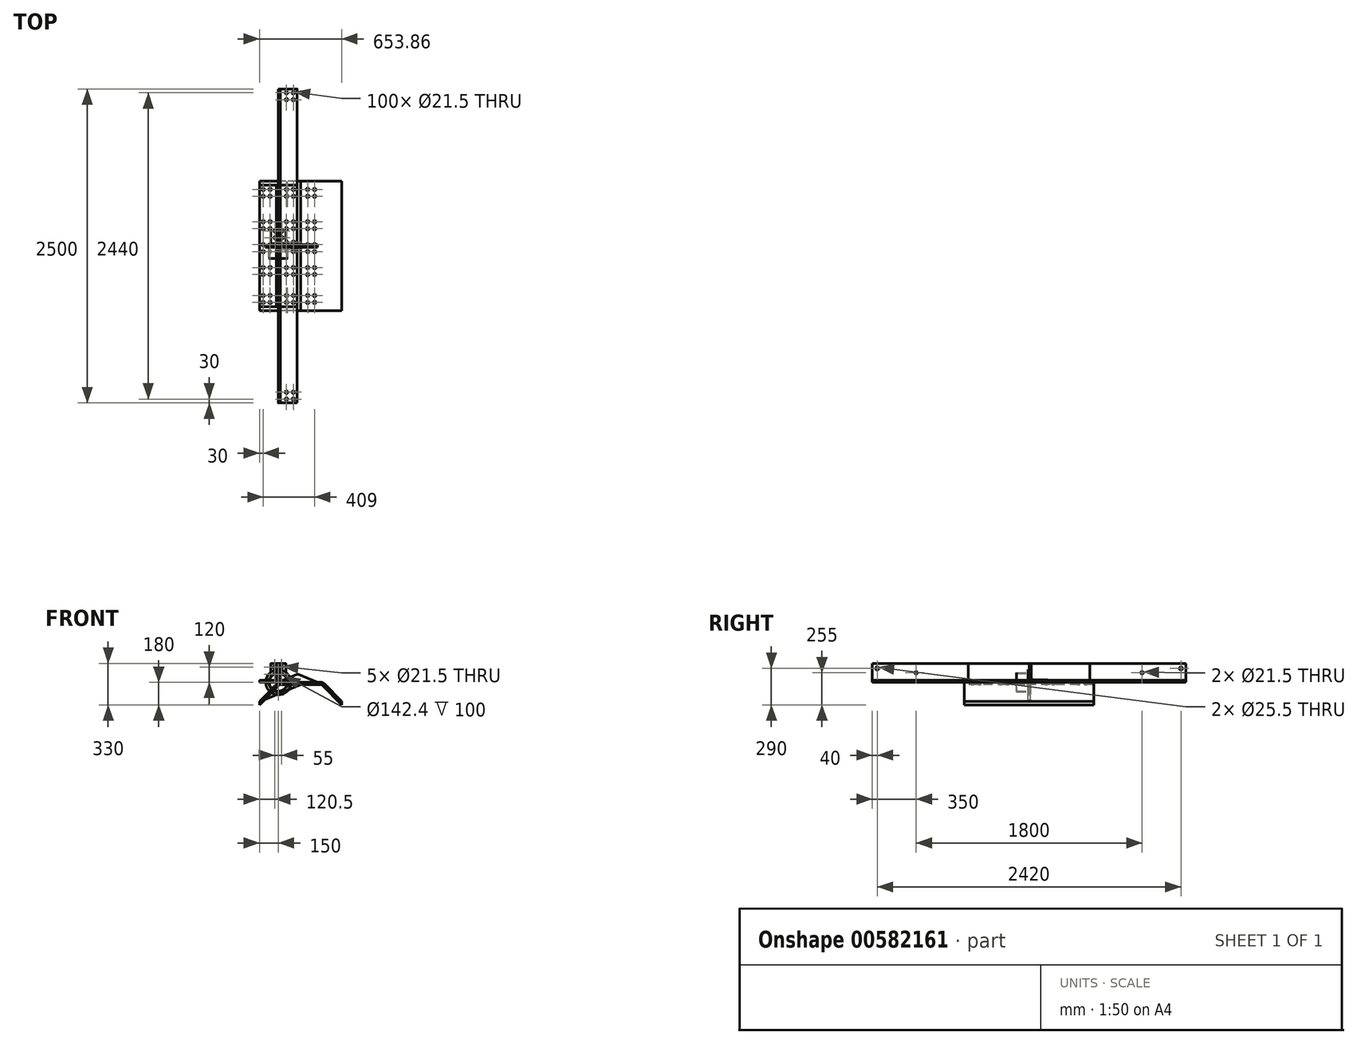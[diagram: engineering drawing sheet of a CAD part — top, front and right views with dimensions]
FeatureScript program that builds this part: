
annotation { "Feature Type Name" : "Feature", "Feature Type Description" : "" }
export const myFeature = defineFeature(function(context is Context, id is Id, definition is map)
    precondition{}
    {
        {
            var Q0;
            Q0=qCreatedBy(makeId("Front.planeOp"),FACE);
            var sketch = newSketch(context, id + "F0", { "sketchPlane" : qUnion([Q0])});
            skLineSegment(sketch, "E0", {"start": v(0, 0) * mm, "end": v(0, 145) * mm});
            skLineSegment(sketch, "E1", {"start": v(0, 0) * mm, "end": v(145, 0) * mm});
            skLineSegment(sketch, "E2", {"start": v(150, 5) * mm, "end": v(150, 10) * mm});
            skLineSegment(sketch, "E3", {"start": v(145, 15) * mm, "end": v(35, 15) * mm});
            skLineSegment(sketch, "E4", {"start": v(15, 35) * mm, "end": v(15, 145) * mm});
            skLineSegment(sketch, "E5", {"start": v(10, 150) * mm, "end": v(5, 150) * mm});
            skPoint(sketch, "E6.visualSharp", {"position": v(15, 15) * mm});
            skArc(sketch, "E6.filletArc", {"start": v(15, 35) * mm, "mid": v(20.86, 20.86) * mm, "end": v(35, 15) * mm});
            skPoint(sketch, "E7.visualSharp", {"position": v(0, 150) * mm});
            skArc(sketch, "E7.filletArc", {"start": v(5, 150) * mm, "mid": v(1.46, 148.54) * mm, "end": v(0, 145) * mm});
            skPoint(sketch, "E8.visualSharp", {"position": v(15, 150) * mm});
            skArc(sketch, "E8.filletArc", {"start": v(15, 145) * mm, "mid": v(13.54, 148.54) * mm, "end": v(10, 150) * mm});
            skPoint(sketch, "E9.visualSharp", {"position": v(150, 15) * mm});
            skArc(sketch, "E9.filletArc", {"start": v(150, 10) * mm, "mid": v(148.54, 13.54) * mm, "end": v(145, 15) * mm});
            skPoint(sketch, "E10.visualSharp", {"position": v(150, 0) * mm});
            skArc(sketch, "E10.filletArc", {"start": v(145, 0) * mm, "mid": v(148.54, 1.46) * mm, "end": v(150, 5) * mm});
            skSolve(sketch);
        }
        {
            var Q0;
            Q0=makeQuery(id+"F0.imprint","IMPRINT",FACE,{"disambiguationData":[TD([[makeQuery(id+"F0.imprint","IMPRINT",EDGE,{"derivedFrom":sQuery(id+"F0.wireOp",EDGE,"E0")}),-1.0]])]});
            extrude(context, id + "F1", {"entities" : qUnion([Q0]), "endBound" : BoundingType.SYMMETRIC, "depth" : 968 * mm, "offsetDistance" : 25 * mm});
        }
        {
            var Q0;
            Q0=qCreatedBy(makeId("Top.planeOp"),FACE);
            var sketch = newSketch(context, id + "F2", { "sketchPlane" : qUnion([Q0])});
            skLineSegment(sketch, "E11", {"start": v(65, -476.9) * mm, "end": v(65, 500.9) * mm});
            skLineSegment(sketch, "E12", {"start": v(120, -552.3) * mm, "end": v(120, 547.64) * mm});
            skLineSegment(sketch, "E13", {"start": v(184.91, -450) * mm, "end": v(-39.38, -450) * mm});
            skLineSegment(sketch, "E14", {"start": v(-37.47, -395) * mm, "end": v(183, -395) * mm});
            skLineSegment(sketch, "E15", {"start": v(183.02, -227.5) * mm, "end": v(-41.27, -227.5) * mm});
            skLineSegment(sketch, "E16", {"start": v(-39.36, -172.5) * mm, "end": v(181.1, -172.5) * mm});
            skLineSegment(sketch, "E17", {"start": v(186.82, 137.5) * mm, "end": v(-37.47, 137.5) * mm});
            skLineSegment(sketch, "E18", {"start": v(-35.56, 192.5) * mm, "end": v(184.91, 192.5) * mm});
            skLineSegment(sketch, "E19", {"start": v(181.72, 395) * mm, "end": v(-42.57, 395) * mm});
            skLineSegment(sketch, "E20", {"start": v(-40.66, 450) * mm, "end": v(179.8, 450) * mm});
            skLineSegment(sketch, "E21", {"start": v(184.27, -45) * mm, "end": v(-40.03, -45) * mm});
            skLineSegment(sketch, "E22", {"start": v(-38.11, 10) * mm, "end": v(182.36, 10) * mm});
            skPoint(sketch, "E23", {"position": v(65, -450) * mm});
            skPoint(sketch, "E24", {"position": v(120, -450) * mm});
            skPoint(sketch, "E25", {"position": v(120, -395) * mm});
            skPoint(sketch, "E26", {"position": v(65, -395) * mm});
            skPoint(sketch, "E27", {"position": v(65, -227.5) * mm});
            skPoint(sketch, "E28", {"position": v(120, -227.5) * mm});
            skPoint(sketch, "E29", {"position": v(120, -172.5) * mm});
            skPoint(sketch, "E30", {"position": v(65, -172.5) * mm});
            skPoint(sketch, "E31", {"position": v(65, -45) * mm});
            skPoint(sketch, "E32", {"position": v(120, -45) * mm});
            skPoint(sketch, "E33", {"position": v(65, 10) * mm});
            skPoint(sketch, "E34", {"position": v(120, 10) * mm});
            skPoint(sketch, "E35", {"position": v(65, 137.5) * mm});
            skPoint(sketch, "E36", {"position": v(65, 192.5) * mm});
            skPoint(sketch, "E37", {"position": v(120, 192.5) * mm});
            skPoint(sketch, "E38", {"position": v(120, 137.5) * mm});
            skPoint(sketch, "E39", {"position": v(65, 395) * mm});
            skPoint(sketch, "E40", {"position": v(120, 395) * mm});
            skPoint(sketch, "E41", {"position": v(120, 450) * mm});
            skPoint(sketch, "E42", {"position": v(65, 450) * mm});
            skSolve(sketch);
        }
        {
            var Q0;
            Q0=sQuery(id+"F2.wireOp",VERTEX,"E23");
            var Q1;
            Q1=sQuery(id+"F2.wireOp",VERTEX,"E26");
            var Q2;
            Q2=sQuery(id+"F2.wireOp",VERTEX,"E25");
            var Q3;
            Q3=sQuery(id+"F2.wireOp",VERTEX,"E24");
            var Q4;
            Q4=sQuery(id+"F2.wireOp",VERTEX,"E27");
            var Q5;
            Q5=sQuery(id+"F2.wireOp",VERTEX,"E28");
            var Q6;
            Q6=sQuery(id+"F2.wireOp",VERTEX,"E29");
            var Q7;
            Q7=sQuery(id+"F2.wireOp",VERTEX,"E30");
            var Q8;
            Q8=sQuery(id+"F2.wireOp",VERTEX,"E31");
            var Q9;
            Q9=sQuery(id+"F2.wireOp",VERTEX,"E33");
            var Q10;
            Q10=sQuery(id+"F2.wireOp",VERTEX,"E34");
            var Q11;
            Q11=sQuery(id+"F2.wireOp",VERTEX,"E32");
            var Q12;
            Q12=sQuery(id+"F2.wireOp",VERTEX,"E35");
            var Q13;
            Q13=sQuery(id+"F2.wireOp",VERTEX,"E38");
            var Q14;
            Q14=sQuery(id+"F2.wireOp",VERTEX,"E37");
            var Q15;
            Q15=sQuery(id+"F2.wireOp",VERTEX,"E36");
            var Q16;
            Q16=sQuery(id+"F2.wireOp",VERTEX,"E39");
            var Q17;
            Q17=sQuery(id+"F2.wireOp",VERTEX,"E40");
            var Q18;
            Q18=sQuery(id+"F2.wireOp",VERTEX,"E42");
            var Q19;
            Q19=sQuery(id+"F2.wireOp",VERTEX,"E41");
            var Q20;
            Q20=makeQuery(id+"F1.opExtrude","SWEPT_BODY",BODY,{"disambiguationData":[OSD([sQuery(id+"F0.wireOp",EDGE,"E0"),sQuery(id+"F0.wireOp",EDGE,"E1"),sQuery(id+"F0.wireOp",EDGE,"E2"),sQuery(id+"F0.wireOp",EDGE,"E3"),sQuery(id+"F0.wireOp",EDGE,"E4"),sQuery(id+"F0.wireOp",EDGE,"E5"),sQuery(id+"F0.wireOp",EDGE,"E6.filletArc"),sQuery(id+"F0.wireOp",EDGE,"E7.filletArc"),sQuery(id+"F0.wireOp",EDGE,"E8.filletArc"),sQuery(id+"F0.wireOp",EDGE,"E9.filletArc"),sQuery(id+"F0.wireOp",EDGE,"E10.filletArc")])]});
            hole(context, id + "F3", {"style" : HoleStyle.SIMPLE, "endStyle" : HoleEndStyle.THROUGH, "oppositeDirection" : true, "holeDiameter" : 21.5 * mm, "majorDiameter" : 5 * mm, "isTappedThrough" : true, "tappedDepth" : 12 * mm, "tapClearance" : 3, "startFromSketch" : true, "locations" : qUnion([Q0, Q1, Q2, Q3, Q4, Q5, Q6, Q7, Q8, Q9, Q10, Q11, Q12, Q13, Q14, Q15, Q16, Q17, Q18, Q19]), "scope" : qUnion([Q20])});
        }
        {
            var Q0;
            Q0=makeQuery(id+"F1.opExtrude","SWEPT_BODY",BODY,{"disambiguationData":[OSD([sQuery(id+"F0.wireOp",EDGE,"E0"),sQuery(id+"F0.wireOp",EDGE,"E1"),sQuery(id+"F0.wireOp",EDGE,"E2"),sQuery(id+"F0.wireOp",EDGE,"E3"),sQuery(id+"F0.wireOp",EDGE,"E4"),sQuery(id+"F0.wireOp",EDGE,"E5"),sQuery(id+"F0.wireOp",EDGE,"E6.filletArc"),sQuery(id+"F0.wireOp",EDGE,"E7.filletArc"),sQuery(id+"F0.wireOp",EDGE,"E8.filletArc"),sQuery(id+"F0.wireOp",EDGE,"E9.filletArc"),sQuery(id+"F0.wireOp",EDGE,"E10.filletArc")])]});
            var Q1;
            Q1=qCreatedBy(makeId("Right.planeOp"),FACE);
            mirror(context, id + "F4", {"entities" : qUnion([Q0]), "mirrorPlane" : qUnion([Q1])});
        }
        {
            var Q0;
            Q0=makeQuery(id+"F1.opExtrude","SWEPT_BODY",BODY,{"disambiguationData":[OSD([sQuery(id+"F0.wireOp",EDGE,"E0"),sQuery(id+"F0.wireOp",EDGE,"E1"),sQuery(id+"F0.wireOp",EDGE,"E2"),sQuery(id+"F0.wireOp",EDGE,"E3"),sQuery(id+"F0.wireOp",EDGE,"E4"),sQuery(id+"F0.wireOp",EDGE,"E5"),sQuery(id+"F0.wireOp",EDGE,"E6.filletArc"),sQuery(id+"F0.wireOp",EDGE,"E7.filletArc"),sQuery(id+"F0.wireOp",EDGE,"E8.filletArc"),sQuery(id+"F0.wireOp",EDGE,"E9.filletArc"),sQuery(id+"F0.wireOp",EDGE,"E10.filletArc")])]});
            transform(context, id + "F5", {"entities" : qUnion([Q0]), "transformType" : TransformType.TRANSLATION_3D, "dx" : 500 * mm, "dy" : 0 * mm, "dz" : 0 * mm, "makeCopy" : true});
        }
        {
            var Q0;
            Q0=makeQuery(id+"F5.opPattern","COPY",BODY,{"derivedFrom":makeQuery(id+"F1.opExtrude","SWEPT_BODY",BODY,{"disambiguationData":[OSD([sQuery(id+"F0.wireOp",EDGE,"E0"),sQuery(id+"F0.wireOp",EDGE,"E1"),sQuery(id+"F0.wireOp",EDGE,"E2"),sQuery(id+"F0.wireOp",EDGE,"E3"),sQuery(id+"F0.wireOp",EDGE,"E4"),sQuery(id+"F0.wireOp",EDGE,"E5"),sQuery(id+"F0.wireOp",EDGE,"E6.filletArc"),sQuery(id+"F0.wireOp",EDGE,"E7.filletArc"),sQuery(id+"F0.wireOp",EDGE,"E8.filletArc"),sQuery(id+"F0.wireOp",EDGE,"E9.filletArc"),sQuery(id+"F0.wireOp",EDGE,"E10.filletArc")])]}),"instanceName":"1"});
            deleteBodies(context, id + "F6", {"entities" : qUnion([Q0])});
        }
        {
            var Q0;
            Q0=makeQuery(id+"F0.imprint","IMPRINT",FACE,{"disambiguationData":[TD([[makeQuery(id+"F0.imprint","IMPRINT",EDGE,{"derivedFrom":sQuery(id+"F0.wireOp",EDGE,"E0")}),-1.0]])]});
            extrude(context, id + "F7", {"entities" : qUnion([Q0]), "endBound" : BoundingType.SYMMETRIC, "depth" : 2500 * mm, "offsetDistance" : 25 * mm});
        }
        {
            var Q0;
            Q0=qCreatedBy(makeId("Top.planeOp"),FACE);
            var sketch = newSketch(context, id + "F8", { "sketchPlane" : qUnion([Q0])});
            skLineSegment(sketch, "E43", {"start": v(65, -1246.9) * mm, "end": v(65, 1291.05) * mm});
            skLineSegment(sketch, "E44", {"start": v(120, -1322.3) * mm, "end": v(120, 1283.3) * mm});
            skLineSegment(sketch, "E45", {"start": v(195.65, -1220) * mm, "end": v(-28.65, -1220) * mm});
            skLineSegment(sketch, "E46", {"start": v(-26.74, -1165) * mm, "end": v(193.74, -1165) * mm});
            skPoint(sketch, "E47", {"position": v(65, -1220) * mm});
            skPoint(sketch, "E48", {"position": v(120, -1220) * mm});
            skPoint(sketch, "E49", {"position": v(120, -1165) * mm});
            skPoint(sketch, "E50", {"position": v(65, -1165) * mm});
            skLineSegment(sketch, "E51", {"start": v(195.65, -30) * mm, "end": v(-28.65, -30) * mm});
            skLineSegment(sketch, "E52", {"start": v(-26.74, 30) * mm, "end": v(193.74, 30) * mm});
            skPoint(sketch, "E53", {"position": v(65, -30) * mm});
            skPoint(sketch, "E54", {"position": v(120, -30) * mm});
            skPoint(sketch, "E55", {"position": v(120, 30) * mm});
            skPoint(sketch, "E56", {"position": v(65, 30) * mm});
            skLineSegment(sketch, "E57", {"start": v(195.65, 1165) * mm, "end": v(-28.65, 1165) * mm});
            skLineSegment(sketch, "E58", {"start": v(-26.74, 1220) * mm, "end": v(193.74, 1220) * mm});
            skPoint(sketch, "E59", {"position": v(65, 1165) * mm});
            skPoint(sketch, "E60", {"position": v(120, 1165) * mm});
            skPoint(sketch, "E61", {"position": v(120, 1220) * mm});
            skPoint(sketch, "E62", {"position": v(65, 1220) * mm});
            skSolve(sketch);
        }
        {
            var Q0;
            Q0=sQuery(id+"F8.wireOp",VERTEX,"E48");
            var Q1;
            Q1=sQuery(id+"F8.wireOp",VERTEX,"E47");
            var Q2;
            Q2=sQuery(id+"F8.wireOp",VERTEX,"E50");
            var Q3;
            Q3=sQuery(id+"F8.wireOp",VERTEX,"E49");
            var Q4;
            Q4=sQuery(id+"F8.wireOp",VERTEX,"E53");
            var Q5;
            Q5=sQuery(id+"F8.wireOp",VERTEX,"E56");
            var Q6;
            Q6=sQuery(id+"F8.wireOp",VERTEX,"E55");
            var Q7;
            Q7=sQuery(id+"F8.wireOp",VERTEX,"E54");
            var Q8;
            Q8=sQuery(id+"F8.wireOp",VERTEX,"E62");
            var Q9;
            Q9=sQuery(id+"F8.wireOp",VERTEX,"E61");
            var Q10;
            Q10=sQuery(id+"F8.wireOp",VERTEX,"E60");
            var Q11;
            Q11=sQuery(id+"F8.wireOp",VERTEX,"E59");
            var Q12;
            Q12=makeQuery(id+"F7.opExtrude","SWEPT_BODY",BODY,{"disambiguationData":[OSD([sQuery(id+"F0.wireOp",EDGE,"E0"),sQuery(id+"F0.wireOp",EDGE,"E1"),sQuery(id+"F0.wireOp",EDGE,"E2"),sQuery(id+"F0.wireOp",EDGE,"E3"),sQuery(id+"F0.wireOp",EDGE,"E4"),sQuery(id+"F0.wireOp",EDGE,"E5"),sQuery(id+"F0.wireOp",EDGE,"E6.filletArc"),sQuery(id+"F0.wireOp",EDGE,"E7.filletArc"),sQuery(id+"F0.wireOp",EDGE,"E8.filletArc"),sQuery(id+"F0.wireOp",EDGE,"E9.filletArc"),sQuery(id+"F0.wireOp",EDGE,"E10.filletArc")])]});
            hole(context, id + "F9", {"style" : HoleStyle.SIMPLE, "endStyle" : HoleEndStyle.THROUGH, "oppositeDirection" : true, "holeDiameter" : 21.5 * mm, "majorDiameter" : 5 * mm, "isTappedThrough" : true, "tappedDepth" : 12 * mm, "tapClearance" : 3, "startFromSketch" : true, "locations" : qUnion([Q0, Q1, Q2, Q3, Q4, Q5, Q6, Q7, Q8, Q9, Q10, Q11]), "scope" : qUnion([Q12])});
        }
        {
            var Q0;
            Q0=qCreatedBy(makeId("Right.planeOp"),FACE);
            var sketch = newSketch(context, id + "F10", { "sketchPlane" : qUnion([Q0])});
            skLineSegment(sketch, "E63", {"start": v(-1210, 110) * mm, "end": v(-1210, 75) * mm});
            skLineSegment(sketch, "E64", {"start": v(-1210, 75) * mm, "end": v(-900, 75) * mm});
            skLineSegment(sketch, "E65", {"start": v(-900, 75) * mm, "end": v(-900, 110) * mm});
            skLineSegment(sketch, "E66", {"start": v(-900, 110) * mm, "end": v(900, 110) * mm});
            skLineSegment(sketch, "E67", {"start": v(900, 110) * mm, "end": v(900, 75) * mm});
            skLineSegment(sketch, "E68", {"start": v(900, 75) * mm, "end": v(1210, 75) * mm});
            skLineSegment(sketch, "E69", {"start": v(1210, 75) * mm, "end": v(1210, 110) * mm});
            skPoint(sketch, "E70", {"position": v(-1210, 110) * mm});
            skPoint(sketch, "E71", {"position": v(-900, 75) * mm});
            skPoint(sketch, "E72", {"position": v(900, 75) * mm});
            skPoint(sketch, "E73", {"position": v(1210, 110) * mm});
            skSolve(sketch);
        }
        {
            var Q0;
            Q0=sQuery(id+"F10.wireOp",VERTEX,"E68.start");
            var Q1;
            Q1=sQuery(id+"F10.wireOp",VERTEX,"E71");
            var Q2;
            Q2=makeQuery(id+"F7.opExtrude","SWEPT_BODY",BODY,{"disambiguationData":[OSD([sQuery(id+"F0.wireOp",EDGE,"E0"),sQuery(id+"F0.wireOp",EDGE,"E1"),sQuery(id+"F0.wireOp",EDGE,"E2"),sQuery(id+"F0.wireOp",EDGE,"E3"),sQuery(id+"F0.wireOp",EDGE,"E4"),sQuery(id+"F0.wireOp",EDGE,"E5"),sQuery(id+"F0.wireOp",EDGE,"E6.filletArc"),sQuery(id+"F0.wireOp",EDGE,"E7.filletArc"),sQuery(id+"F0.wireOp",EDGE,"E8.filletArc"),sQuery(id+"F0.wireOp",EDGE,"E9.filletArc"),sQuery(id+"F0.wireOp",EDGE,"E10.filletArc")])]});
            hole(context, id + "F11", {"style" : HoleStyle.SIMPLE, "endStyle" : HoleEndStyle.THROUGH, "oppositeDirection" : true, "holeDiameter" : 21.5 * mm, "majorDiameter" : 5 * mm, "isTappedThrough" : true, "tappedDepth" : 12 * mm, "tapClearance" : 3, "startFromSketch" : true, "locations" : qUnion([Q0, Q1]), "scope" : qUnion([Q2])});
        }
        {
            var Q0;
            Q0=sQuery(id+"F10.wireOp",VERTEX,"E63.start");
            var Q1;
            Q1=sQuery(id+"F10.wireOp",VERTEX,"E73");
            var Q2;
            Q2=makeQuery(id+"F7.opExtrude","SWEPT_BODY",BODY,{"disambiguationData":[OSD([sQuery(id+"F0.wireOp",EDGE,"E0"),sQuery(id+"F0.wireOp",EDGE,"E1"),sQuery(id+"F0.wireOp",EDGE,"E2"),sQuery(id+"F0.wireOp",EDGE,"E3"),sQuery(id+"F0.wireOp",EDGE,"E4"),sQuery(id+"F0.wireOp",EDGE,"E5"),sQuery(id+"F0.wireOp",EDGE,"E6.filletArc"),sQuery(id+"F0.wireOp",EDGE,"E7.filletArc"),sQuery(id+"F0.wireOp",EDGE,"E8.filletArc"),sQuery(id+"F0.wireOp",EDGE,"E9.filletArc"),sQuery(id+"F0.wireOp",EDGE,"E10.filletArc")])]});
            hole(context, id + "F12", {"style" : HoleStyle.SIMPLE, "endStyle" : HoleEndStyle.THROUGH, "oppositeDirection" : true, "holeDiameter" : 25.5 * mm, "majorDiameter" : 5 * mm, "isTappedThrough" : true, "tappedDepth" : 12 * mm, "tapClearance" : 3, "startFromSketch" : true, "locations" : qUnion([Q0, Q1]), "scope" : qUnion([Q2])});
        }
        {
            var Q0;
            Q0=qCreatedBy(makeId("Front.planeOp"),FACE);
            var sketch = newSketch(context, id + "F13", { "sketchPlane" : qUnion([Q0])});
            skLineSegment(sketch, "E74", {"start": v(0, 97) * mm, "end": v(0, 0) * mm});
            skLineSegment(sketch, "E75", {"start": v(0, 0) * mm, "end": v(97, 0) * mm});
            skLineSegment(sketch, "E76", {"start": v(100, 3) * mm, "end": v(100, 7) * mm});
            skLineSegment(sketch, "E77", {"start": v(97, 10) * mm, "end": v(22, 10) * mm});
            skLineSegment(sketch, "E78", {"start": v(10, 22) * mm, "end": v(10, 97) * mm});
            skLineSegment(sketch, "E79", {"start": v(7, 100) * mm, "end": v(3, 100) * mm});
            skPoint(sketch, "E80.visualSharp", {"position": v(0, 100) * mm});
            skArc(sketch, "E80.filletArc", {"start": v(3, 100) * mm, "mid": v(0.88, 99.12) * mm, "end": v(0, 97) * mm});
            skPoint(sketch, "E81.visualSharp", {"position": v(10, 100) * mm});
            skArc(sketch, "E81.filletArc", {"start": v(10, 97) * mm, "mid": v(9.12, 99.12) * mm, "end": v(7, 100) * mm});
            skPoint(sketch, "E82.visualSharp", {"position": v(100, 10) * mm});
            skArc(sketch, "E82.filletArc", {"start": v(100, 7) * mm, "mid": v(99.12, 9.12) * mm, "end": v(97, 10) * mm});
            skPoint(sketch, "E83.visualSharp", {"position": v(100, 0) * mm});
            skArc(sketch, "E83.filletArc", {"start": v(97, 0) * mm, "mid": v(99.12, 0.88) * mm, "end": v(100, 3) * mm});
            skPoint(sketch, "E84.visualSharp", {"position": v(10, 10) * mm});
            skArc(sketch, "E84.filletArc", {"start": v(10, 22) * mm, "mid": v(13.51, 13.51) * mm, "end": v(22, 10) * mm});
            skSolve(sketch);
        }
        {
            var Q0;
            Q0=makeQuery(id+"F13.imprint","IMPRINT",FACE,{"disambiguationData":[TD([[makeQuery(id+"F13.imprint","IMPRINT",EDGE,{"derivedFrom":sQuery(id+"F13.wireOp",EDGE,"E74")}),1.0]])]});
            extrude(context, id + "F14", {"entities" : qUnion([Q0]), "endBound" : BoundingType.SYMMETRIC, "depth" : 968 * mm, "offsetDistance" : 25 * mm});
        }
        {
            var Q0;
            Q0=qCreatedBy(makeId("Top.planeOp"),FACE);
            var sketch = newSketch(context, id + "F15", { "sketchPlane" : qUnion([Q0])});
            skLineSegment(sketch, "E85", {"start": v(0, 450) * mm, "end": v(72.5, 450) * mm});
            skLineSegment(sketch, "E86", {"start": v(72.5, 450) * mm, "end": v(72.5, 395) * mm});
            skLineSegment(sketch, "E87", {"start": v(72.5, 395) * mm, "end": v(0, 395) * mm});
            skLineSegment(sketch, "E88", {"start": v(0, 395) * mm, "end": v(0, -395) * mm});
            skLineSegment(sketch, "E89", {"start": v(0, -395) * mm, "end": v(72.5, -395) * mm});
            skLineSegment(sketch, "E90", {"start": v(72.5, -395) * mm, "end": v(72.5, -450) * mm});
            skPoint(sketch, "E91", {"position": v(72.5, -395) * mm});
            skPoint(sketch, "E92", {"position": v(72.5, -450) * mm});
            skPoint(sketch, "E93", {"position": v(72.5, 395) * mm});
            skPoint(sketch, "E94", {"position": v(72.5, 450) * mm});
            skSolve(sketch);
        }
        {
            var Q0;
            Q0=sQuery(id+"F15.wireOp",VERTEX,"E85.end");
            var Q1;
            Q1=sQuery(id+"F15.wireOp",VERTEX,"E93");
            var Q2;
            Q2=sQuery(id+"F15.wireOp",VERTEX,"E91");
            var Q3;
            Q3=sQuery(id+"F15.wireOp",VERTEX,"E92");
            var Q4;
            Q4=makeQuery(id+"F14.opExtrude","SWEPT_BODY",BODY,{"disambiguationData":[OSD([sQuery(id+"F13.wireOp",EDGE,"E74"),sQuery(id+"F13.wireOp",EDGE,"E75"),sQuery(id+"F13.wireOp",EDGE,"E76"),sQuery(id+"F13.wireOp",EDGE,"E77"),sQuery(id+"F13.wireOp",EDGE,"E78"),sQuery(id+"F13.wireOp",EDGE,"E79"),sQuery(id+"F13.wireOp",EDGE,"E80.filletArc"),sQuery(id+"F13.wireOp",EDGE,"E81.filletArc"),sQuery(id+"F13.wireOp",EDGE,"E82.filletArc"),sQuery(id+"F13.wireOp",EDGE,"E83.filletArc"),sQuery(id+"F13.wireOp",EDGE,"E84.filletArc")])]});
            hole(context, id + "F16", {"style" : HoleStyle.SIMPLE, "endStyle" : HoleEndStyle.THROUGH, "oppositeDirection" : true, "holeDiameter" : 21.5 * mm, "majorDiameter" : 5 * mm, "isTappedThrough" : true, "tappedDepth" : 12 * mm, "tapClearance" : 3, "startFromSketch" : true, "locations" : qUnion([Q0, Q1, Q2, Q3]), "scope" : qUnion([Q4])});
        }
        {
            var Q0;
            Q0=qCreatedBy(makeId("Right.planeOp"),FACE);
            var sketch = newSketch(context, id + "F17", { "sketchPlane" : qUnion([Q0])});
            skLineSegment(sketch, "E95", {"start": v(0, 0) * mm, "end": v(145, 0) * mm});
            skLineSegment(sketch, "E96", {"start": v(150, 5) * mm, "end": v(150, 13) * mm});
            skLineSegment(sketch, "E97", {"start": v(145, 18) * mm, "end": v(38, 18) * mm});
            skLineSegment(sketch, "E98", {"start": v(18, 38) * mm, "end": v(18, 145) * mm});
            skLineSegment(sketch, "E99", {"start": v(13, 150) * mm, "end": v(5, 150) * mm});
            skLineSegment(sketch, "E100", {"start": v(0, 145) * mm, "end": v(0, 0) * mm});
            skPoint(sketch, "E101.visualSharp", {"position": v(0, 150) * mm});
            skArc(sketch, "E101.filletArc", {"start": v(5, 150) * mm, "mid": v(1.46, 148.54) * mm, "end": v(0, 145) * mm});
            skPoint(sketch, "E102.visualSharp", {"position": v(18, 150) * mm});
            skArc(sketch, "E102.filletArc", {"start": v(18, 145) * mm, "mid": v(16.54, 148.54) * mm, "end": v(13, 150) * mm});
            skPoint(sketch, "E103.visualSharp", {"position": v(150, 18) * mm});
            skArc(sketch, "E103.filletArc", {"start": v(150, 13) * mm, "mid": v(148.54, 16.54) * mm, "end": v(145, 18) * mm});
            skPoint(sketch, "E104.visualSharp", {"position": v(150, 0) * mm});
            skArc(sketch, "E104.filletArc", {"start": v(145, 0) * mm, "mid": v(148.54, 1.46) * mm, "end": v(150, 5) * mm});
            skPoint(sketch, "E105.visualSharp", {"position": v(18, 18) * mm});
            skArc(sketch, "E105.filletArc", {"start": v(18, 38) * mm, "mid": v(23.86, 23.86) * mm, "end": v(38, 18) * mm});
            skSolve(sketch);
        }
        {
            var Q0;
            Q0=makeQuery(id+"F17.imprint","IMPRINT",FACE,{"disambiguationData":[TD([[makeQuery(id+"F17.imprint","IMPRINT",EDGE,{"derivedFrom":sQuery(id+"F17.wireOp",EDGE,"E95")}),1.0]])]});
            extrude(context, id + "F18", {"entities" : qUnion([Q0]), "endBound" : BoundingType.SYMMETRIC, "oppositeDirection" : true, "depth" : 119 * mm, "offsetDistance" : 25 * mm});
        }
        {
            var Q0;
            Q0=qCreatedBy(makeId("Front.planeOp"),FACE);
            var sketch = newSketch(context, id + "F19", { "sketchPlane" : qUnion([Q0])});
            skLineSegment(sketch, "E106", {"start": v(-29.5, 0) * mm, "end": v(-29.5, 65) * mm});
            skLineSegment(sketch, "E107", {"start": v(-29.5, 65) * mm, "end": v(25.5, 65) * mm});
            skLineSegment(sketch, "E108", {"start": v(25.5, 65) * mm, "end": v(25.5, 120) * mm});
            skLineSegment(sketch, "E109", {"start": v(25.5, 120) * mm, "end": v(-29.5, 120) * mm});
            skPoint(sketch, "E110", {"position": v(-29.5, 65) * mm});
            skPoint(sketch, "E111", {"position": v(25.5, 65) * mm});
            skPoint(sketch, "E112", {"position": v(25.5, 120) * mm});
            skPoint(sketch, "E113", {"position": v(-29.5, 120) * mm});
            skSolve(sketch);
        }
        {
            var Q0;
            Q0=qCreatedBy(makeId("Top.planeOp"),FACE);
            var sketch = newSketch(context, id + "F20", { "sketchPlane" : qUnion([Q0])});
            skLineSegment(sketch, "E114", {"start": v(29.5, 0) * mm, "end": v(29.5, 65) * mm});
            skLineSegment(sketch, "E115", {"start": v(29.5, 65) * mm, "end": v(-25.5, 65) * mm});
            skLineSegment(sketch, "E116", {"start": v(-25.5, 65) * mm, "end": v(-25.5, 120) * mm});
            skLineSegment(sketch, "E117", {"start": v(-25.5, 120) * mm, "end": v(29.5, 120) * mm});
            skPoint(sketch, "E118", {"position": v(29.5, 120) * mm});
            skPoint(sketch, "E119", {"position": v(-25.5, 120) * mm});
            skPoint(sketch, "E120", {"position": v(-25.5, 65) * mm});
            skPoint(sketch, "E121", {"position": v(29.5, 65) * mm});
            skSolve(sketch);
        }
        {
            var Q0;
            Q0=sQuery(id+"F20.wireOp",VERTEX,"E116.end");
            var Q1;
            Q1=sQuery(id+"F20.wireOp",VERTEX,"E118");
            var Q2;
            Q2=sQuery(id+"F20.wireOp",VERTEX,"E121");
            var Q3;
            Q3=sQuery(id+"F20.wireOp",VERTEX,"E120");
            var Q4;
            Q4=makeQuery(id+"F18.opExtrude","SWEPT_BODY",BODY,{"disambiguationData":[OSD([sQuery(id+"F17.wireOp",EDGE,"E95"),sQuery(id+"F17.wireOp",EDGE,"E96"),sQuery(id+"F17.wireOp",EDGE,"E97"),sQuery(id+"F17.wireOp",EDGE,"E98"),sQuery(id+"F17.wireOp",EDGE,"E99"),sQuery(id+"F17.wireOp",EDGE,"E100"),sQuery(id+"F17.wireOp",EDGE,"E101.filletArc"),sQuery(id+"F17.wireOp",EDGE,"E102.filletArc"),sQuery(id+"F17.wireOp",EDGE,"E103.filletArc"),sQuery(id+"F17.wireOp",EDGE,"E104.filletArc"),sQuery(id+"F17.wireOp",EDGE,"E105.filletArc")])]});
            hole(context, id + "F21", {"style" : HoleStyle.SIMPLE, "endStyle" : HoleEndStyle.THROUGH, "oppositeDirection" : true, "holeDiameter" : 21.5 * mm, "majorDiameter" : 5 * mm, "isTappedThrough" : true, "tappedDepth" : 12 * mm, "tapClearance" : 3, "startFromSketch" : true, "locations" : qUnion([Q0, Q1, Q2, Q3]), "scope" : qUnion([Q4])});
        }
        {
            var Q0;
            Q0=sQuery(id+"F19.wireOp",VERTEX,"E110");
            var Q1;
            Q1=sQuery(id+"F19.wireOp",VERTEX,"E111");
            var Q2;
            Q2=sQuery(id+"F19.wireOp",VERTEX,"E109.start");
            var Q3;
            Q3=sQuery(id+"F19.wireOp",VERTEX,"E113");
            var Q4;
            Q4=makeQuery(id+"F18.opExtrude","SWEPT_BODY",BODY,{"disambiguationData":[OSD([sQuery(id+"F17.wireOp",EDGE,"E95"),sQuery(id+"F17.wireOp",EDGE,"E96"),sQuery(id+"F17.wireOp",EDGE,"E97"),sQuery(id+"F17.wireOp",EDGE,"E98"),sQuery(id+"F17.wireOp",EDGE,"E99"),sQuery(id+"F17.wireOp",EDGE,"E100"),sQuery(id+"F17.wireOp",EDGE,"E101.filletArc"),sQuery(id+"F17.wireOp",EDGE,"E102.filletArc"),sQuery(id+"F17.wireOp",EDGE,"E103.filletArc"),sQuery(id+"F17.wireOp",EDGE,"E104.filletArc"),sQuery(id+"F17.wireOp",EDGE,"E105.filletArc")])]});
            hole(context, id + "F22", {"style" : HoleStyle.SIMPLE, "endStyle" : HoleEndStyle.THROUGH, "holeDiameter" : 21.5 * mm, "majorDiameter" : 5 * mm, "isTappedThrough" : true, "tappedDepth" : 12 * mm, "tapClearance" : 3, "startFromSketch" : true, "locations" : qUnion([Q0, Q1, Q2, Q3]), "scope" : qUnion([Q4])});
        }
        {
            var Q0;
            Q0=qCreatedBy(makeId("Front.planeOp"),FACE);
            var sketch = newSketch(context, id + "F23", { "sketchPlane" : qUnion([Q0])});
            skLineSegment(sketch, "E122", {"start": v(177, 0) * mm, "end": v(177, -20) * mm});
            skLineSegment(sketch, "E123", {"start": v(177, 0) * mm, "end": v(14.77, 0) * mm});
            skLineSegment(sketch, "E124", {"start": v(-149.86, -180) * mm, "end": v(5.57, -22.97) * mm});
            skLineSegment(sketch, "E125", {"start": v(13.38, -45) * mm, "end": v(169.86, -45) * mm});
            skLineSegment(sketch, "E126", {"start": v(-149.86, -151.57) * mm, "end": v(-10.1, -10.38) * mm});
            skLineSegment(sketch, "E127", {"start": v(-149.86, -151.57) * mm, "end": v(-149.86, -180) * mm});
            skLineSegment(sketch, "E128", {"start": v(177, -20) * mm, "end": v(-110.02, -139.75) * mm});
            skLineSegment(sketch, "E129", {"start": v(5.08, -23.47) * mm, "end": v(13.38, -20) * mm});
            skLineSegment(sketch, "E130", {"start": v(5.08, -23.47) * mm, "end": v(-110.02, -139.75) * mm});
            skLineSegment(sketch, "E131", {"start": v(13.38, -20) * mm, "end": v(177, -20) * mm});
            skLineSegment(sketch, "E132", {"start": v(177, -20) * mm, "end": v(12.68, -20) * mm});
            skLineSegment(sketch, "E133", {"start": v(5.08, -23.47) * mm, "end": v(9.23, -21.73) * mm});
            skPoint(sketch, "E134.visualSharp", {"position": v(0.16, 0) * mm});
            skArc(sketch, "E134.filletArc", {"start": v(14.77, 0) * mm, "mid": v(1.3, -2.7) * mm, "end": v(-10.1, -10.38) * mm});
            skPoint(sketch, "E135.visualSharp", {"position": v(8.5, -20) * mm});
            skArc(sketch, "E135.filletArc", {"start": v(12.68, -20) * mm, "mid": v(8.83, -20.77) * mm, "end": v(5.57, -22.97) * mm});
            skSolve(sketch);
        }
        {
            var Q0;
            Q0=makeQuery(id+"F23.imprint","IMPRINT",FACE,{"disambiguationData":[TD([[makeQuery(id+"F23.imprint","IMPRINT",EDGE,{"derivedFrom":sQuery(id+"F23.wireOp",EDGE,"E122")}),-1.0]])]});
            extrude(context, id + "F24", {"entities" : qUnion([Q0]), "endBound" : BoundingType.SYMMETRIC, "oppositeDirection" : true, "depth" : 1030 * mm, "offsetDistance" : 25 * mm});
        }
        {
            var Q0;
            Q0=sQuery(id+"F2.wireOp",VERTEX,"E42");
            var Q1;
            Q1=sQuery(id+"F2.wireOp",VERTEX,"E41");
            var Q2;
            Q2=sQuery(id+"F2.wireOp",VERTEX,"E39");
            var Q3;
            Q3=sQuery(id+"F2.wireOp",VERTEX,"E40");
            var Q4;
            Q4=sQuery(id+"F2.wireOp",VERTEX,"E36");
            var Q5;
            Q5=sQuery(id+"F2.wireOp",VERTEX,"E37");
            var Q6;
            Q6=sQuery(id+"F2.wireOp",VERTEX,"E38");
            var Q7;
            Q7=sQuery(id+"F2.wireOp",VERTEX,"E35");
            var Q8;
            Q8=sQuery(id+"F2.wireOp",VERTEX,"E33");
            var Q9;
            Q9=sQuery(id+"F2.wireOp",VERTEX,"E34");
            var Q10;
            Q10=sQuery(id+"F2.wireOp",VERTEX,"E32");
            var Q11;
            Q11=sQuery(id+"F2.wireOp",VERTEX,"E31");
            var Q12;
            Q12=sQuery(id+"F2.wireOp",VERTEX,"E30");
            var Q13;
            Q13=sQuery(id+"F2.wireOp",VERTEX,"E29");
            var Q14;
            Q14=sQuery(id+"F2.wireOp",VERTEX,"E28");
            var Q15;
            Q15=sQuery(id+"F2.wireOp",VERTEX,"E27");
            var Q16;
            Q16=sQuery(id+"F2.wireOp",VERTEX,"E26");
            var Q17;
            Q17=sQuery(id+"F2.wireOp",VERTEX,"E24");
            var Q18;
            Q18=sQuery(id+"F2.wireOp",VERTEX,"E23");
            var Q19;
            Q19=sQuery(id+"F2.wireOp",VERTEX,"E25");
            var Q20;
            Q20=makeQuery(id+"F24.opExtrude","SWEPT_BODY",BODY,{"disambiguationData":[OSD([sQuery(id+"F23.wireOp",EDGE,"E122"),sQuery(id+"F23.wireOp",EDGE,"E123"),sQuery(id+"F23.wireOp",EDGE,"E124"),sQuery(id+"F23.wireOp",EDGE,"E125"),sQuery(id+"F23.wireOp",EDGE,"E126"),sQuery(id+"F23.wireOp",EDGE,"E127"),sQuery(id+"F23.wireOp",EDGE,"da38f5bd-720c-4174-92c1-8dae11744c1f.filletArc")])]});
            hole(context, id + "F25", {"style" : HoleStyle.SIMPLE, "endStyle" : HoleEndStyle.THROUGH, "holeDiameter" : 21.5 * mm, "majorDiameter" : 5 * mm, "isTappedThrough" : true, "tappedDepth" : 12 * mm, "tapClearance" : 3, "startFromSketch" : true, "locations" : qUnion([Q0, Q1, Q2, Q3, Q4, Q5, Q6, Q7, Q8, Q9, Q10, Q11, Q12, Q13, Q14, Q15, Q16, Q17, Q18, Q19]), "scope" : qUnion([Q20])});
        }
        {
            var Q0;
            Q0=makeQuery(id+"F24.opExtrude","SWEPT_BODY",BODY,{"disambiguationData":[OSD([sQuery(id+"F23.wireOp",EDGE,"E122"),sQuery(id+"F23.wireOp",EDGE,"E123"),sQuery(id+"F23.wireOp",EDGE,"E124"),sQuery(id+"F23.wireOp",EDGE,"E125"),sQuery(id+"F23.wireOp",EDGE,"E126"),sQuery(id+"F23.wireOp",EDGE,"E127"),sQuery(id+"F23.wireOp",EDGE,"da38f5bd-720c-4174-92c1-8dae11744c1f.filletArc")])]});
            var Q1;
            Q1=makeQuery(id+"F24.opExtrude","SWEPT_FACE",FACE,{"disambiguationData":[OSD([sQuery(id+"F23.wireOp",EDGE,"E122")])]});
            mirror(context, id + "F26", {"entities" : qUnion([Q0]), "mirrorPlane" : qUnion([Q1])});
        }
        {
            var Q0;
            Q0=qCreatedBy(makeId("Front.planeOp"),FACE);
            var sketch = newSketch(context, id + "F27", { "sketchPlane" : qUnion([Q0])});
            skCircle(sketch, "E136", {"center": v(0, 0) * mm, "radius": 76.2 * mm});
            skCircle(sketch, "E137", {"center": v(0, 0) * mm, "radius": 71.2 * mm});
            skSolve(sketch);
        }
        {
            var Q0;
            Q0=makeQuery(id+"F27.imprint","IMPRINT",FACE,{"disambiguationData":[TD([[makeQuery(id+"F27.imprint","IMPRINT",EDGE,{"derivedFrom":sQuery(id+"F27.wireOp",EDGE,"E136")}),1.0]])]});
            extrude(context, id + "F28", {"entities" : qUnion([Q0]), "depth" : 100 * mm, "offsetDistance" : 25 * mm});
        }
        {
            var Q0;
            Q0=qCreatedBy(makeId("Front.planeOp"),FACE);
            var sketch = newSketch(context, id + "F29", { "sketchPlane" : qUnion([Q0])});
            skCircle(sketch, "E138", {"center": v(0, 0) * mm, "radius": 100 * mm});
            skCircle(sketch, "E139", {"center": v(0, 0) * mm, "radius": 10.75 * mm});
            skSolve(sketch);
        }
        {
            var Q0;
            Q0=makeQuery(id+"F29.imprint","IMPRINT",FACE,{"disambiguationData":[TD([[makeQuery(id+"F29.imprint","IMPRINT",EDGE,{"derivedFrom":sQuery(id+"F29.wireOp",EDGE,"E138")}),1.0]])]});
            extrude(context, id + "F30", {"entities" : qUnion([Q0]), "depth" : 10 * mm, "offsetDistance" : 25 * mm});
        }
        {
            var Q0;
            Q0=qCreatedBy(makeId("Front.planeOp"),FACE);
            var sketch = newSketch(context, id + "F31", { "sketchPlane" : qUnion([Q0])});
            skLineSegment(sketch, "E140", {"start": v(0, 0) * mm, "end": v(311, 0) * mm});
            skLineSegment(sketch, "E141", {"start": v(0, 0) * mm, "end": v(151, 63) * mm});
            skLineSegment(sketch, "E142", {"start": v(160, 63) * mm, "end": v(311, 0) * mm});
            skLineSegment(sketch, "E143", {"start": v(151, 63) * mm, "end": v(160, 63) * mm});
            skSolve(sketch);
        }
        {
            var Q0;
            Q0=makeQuery(id+"F31.imprint","IMPRINT",FACE,{"disambiguationData":[TD([[makeQuery(id+"F31.imprint","IMPRINT",EDGE,{"derivedFrom":sQuery(id+"F31.wireOp",EDGE,"E140")}),1.0]])]});
            var sketch = newSketch(context, id + "F32", { "sketchPlane" : qUnion([Q0])});
            skSolve(sketch);
        }
        {
            var Q0;
            Q0=makeQuery(id+"F32.imprint","IMPRINT",FACE,{"disambiguationData":[TD([[makeQuery(id+"F32.imprint","IMPRINT",EDGE,{"derivedFrom":makeQuery(id+"F31.imprint","IMPRINT",EDGE,{"derivedFrom":sQuery(id+"F31.wireOp",EDGE,"E140")})}),1.0]])]});
            extrude(context, id + "F33", {"entities" : qUnion([Q0]), "endBound" : BoundingType.SYMMETRIC, "depth" : 20 * mm, "offsetDistance" : 25 * mm});
        }
        {
            var Q0;
            {var subQ3=sQuery(id+"F23.wireOp",EDGE,"E129");Q0=makeQuery(id+"F23.imprint","IMPRINT",FACE,{"disambiguationData":[TD([[makeQuery(id+"F23.imprint","IMPRINT",EDGE,{"derivedFrom":subQ3}),-1.0]])]});}
            extrude(context, id + "F34", {"entities" : qUnion([Q0]), "endBound" : BoundingType.SYMMETRIC, "depth" : 20 * mm, "offsetDistance" : 25 * mm});
        }
    });
